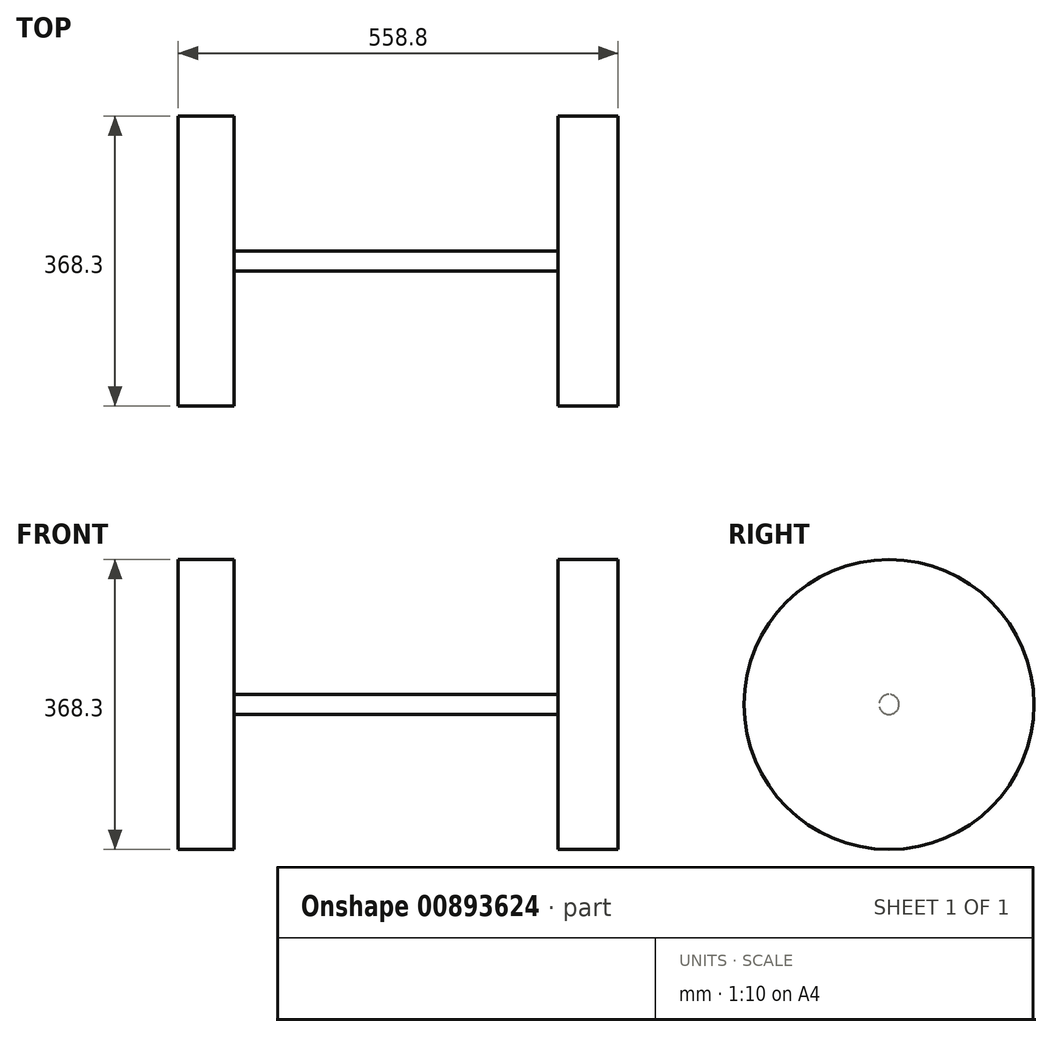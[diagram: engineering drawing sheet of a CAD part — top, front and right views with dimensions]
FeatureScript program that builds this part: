
annotation { "Feature Type Name" : "Feature", "Feature Type Description" : "" }
export const myFeature = defineFeature(function(context is Context, id is Id, definition is map)
    precondition{}
    {
        {
            var Q0;
            Q0=qCreatedBy(makeId("Right.planeOp"),FACE);
            var sketch = newSketch(context, id + "F0", { "sketchPlane" : qUnion([Q0])});
            skCircle(sketch, "E0", {"center": v(0, 0) * mm, "radius": 12.7 * mm});
            skSolve(sketch);
        }
        {
            var Q0;
            Q0=makeQuery(id+"F0.imprint","IMPRINT",FACE,{"disambiguationData":[TD([[makeQuery(id+"F0.imprint","IMPRINT",EDGE,{"derivedFrom":sQuery(id+"F0.wireOp",EDGE,"E0")}),1.0]])]});
            var Q1;
            Q1 = qConstructionFilter(qBodyType(qCreatedBy(id + "F0" ,EDGE), BodyType.WIRE), ConstructionObject.NO);
            extrude(context, id + "F1", {"entities" : qUnion([Q0]), "surfaceEntities" : qUnion([Q1]), "endBound" : BoundingType.SYMMETRIC, "depth" : 558.8 * mm, "offsetDistance" : 25.4 * mm});
        }
        {
            var Q0;
            Q0=makeQuery(id+"F1.opExtrude","CAP_FACE",FACE,{"disambiguationData":[OSD([sQuery(id+"F0.wireOp",EDGE,"E0")])],"isStart":false});
            var sketch = newSketch(context, id + "F2", { "sketchPlane" : qUnion([Q0])});
            skCircle(sketch, "E1", {"center": v(0, 0) * mm, "radius": 184.15 * mm});
            skSolve(sketch);
        }
        {
            var Q0;
            Q0=makeQuery(id+"F2.imprint","IMPRINT",FACE,{"disambiguationData":[TD([[makeQuery(id+"F2.imprint","IMPRINT",EDGE,{"derivedFrom":sQuery(id+"F2.wireOp",EDGE,"E1")}),1.0]])]});
            extrude(context, id + "F3", {"entities" : qUnion([Q0]), "operationType" : NewBodyOperationType.ADD, "oppositeDirection" : true, "depth" : 76.2 * mm, "offsetDistance" : 25.4 * mm});
        }
        {
            var Q0;
            Q0=makeQuery(id+"F1.opExtrude","CAP_FACE",FACE,{"disambiguationData":[OSD([sQuery(id+"F0.wireOp",EDGE,"E0")])],"isStart":true});
            var sketch = newSketch(context, id + "F4", { "sketchPlane" : qUnion([Q0])});
            skCircle(sketch, "E2", {"center": v(0, 0) * mm, "radius": 184.15 * mm});
            skSolve(sketch);
        }
        {
            var Q0;
            Q0=makeQuery(id+"F4.imprint","IMPRINT",FACE,{"disambiguationData":[TD([[makeQuery(id+"F4.imprint","IMPRINT",EDGE,{"derivedFrom":sQuery(id+"F4.wireOp",EDGE,"E2")}),1.0]])]});
            extrude(context, id + "F5", {"entities" : qUnion([Q0]), "operationType" : NewBodyOperationType.ADD, "oppositeDirection" : true, "depth" : 71.12 * mm, "offsetDistance" : 25.4 * mm});
        }
    });
